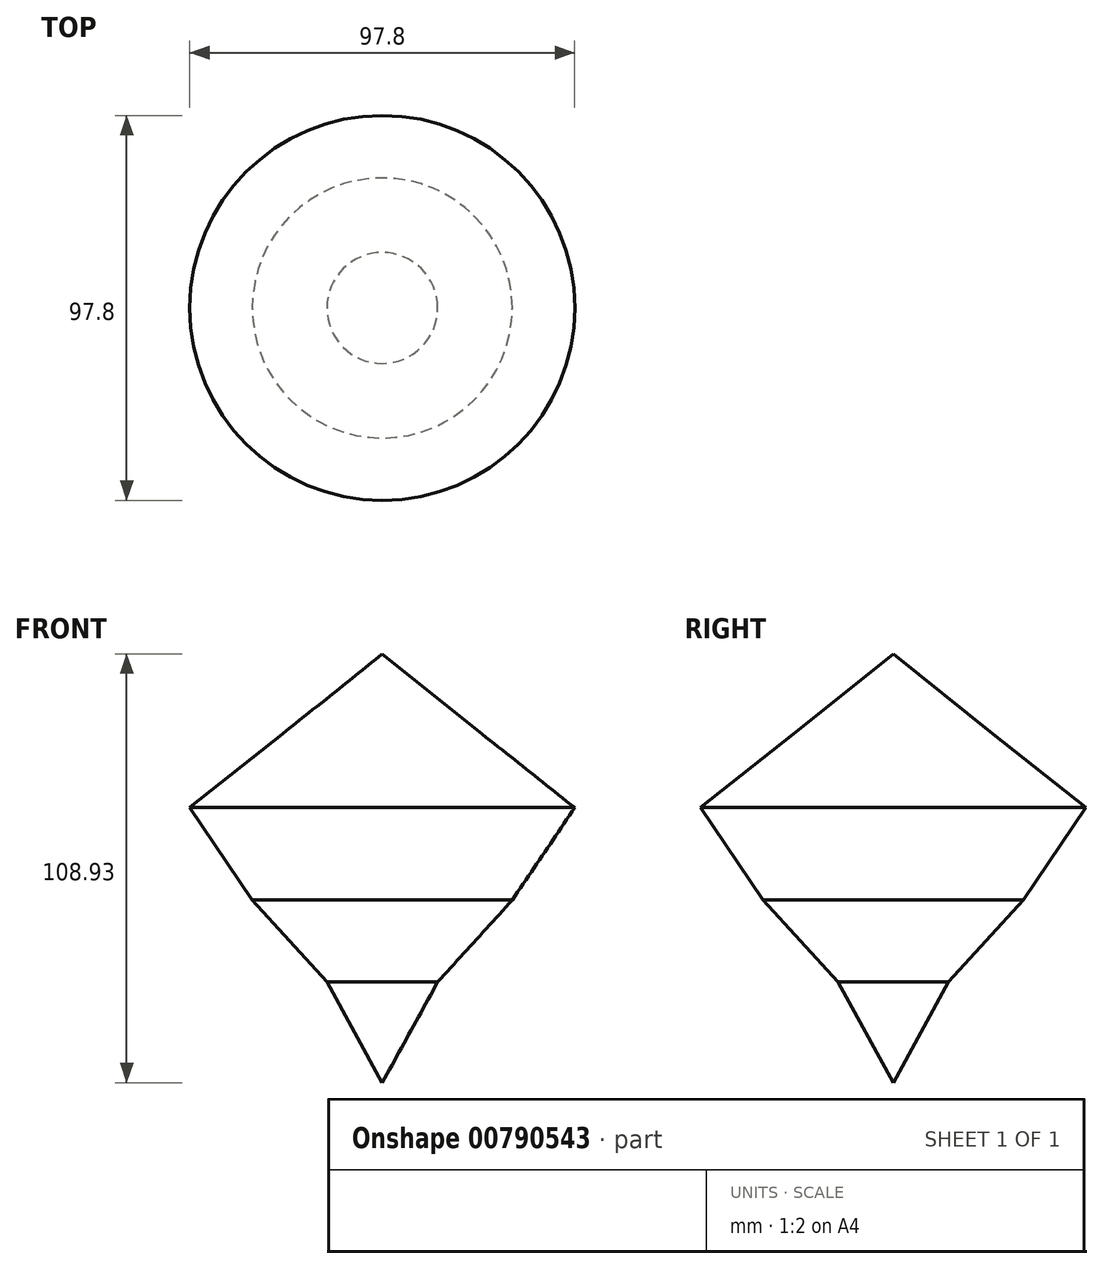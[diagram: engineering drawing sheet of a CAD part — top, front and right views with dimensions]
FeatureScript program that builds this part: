
annotation { "Feature Type Name" : "Feature", "Feature Type Description" : "" }
export const myFeature = defineFeature(function(context is Context, id is Id, definition is map)
    precondition{}
    {
        {
            var Q0;
            Q0=qCreatedBy(makeId("Front.planeOp"),FACE);
            var sketch = newSketch(context, id + "F0", { "sketchPlane" : qUnion([Q0])});
            skLineSegment(sketch, "E0", {"start": v(0, 60.6) * mm, "end": v(0, -48.32) * mm});
            skLineSegment(sketch, "E1", {"start": v(0, 60.6) * mm, "end": v(-25.37, 40.24) * mm});
            skLineSegment(sketch, "E2", {"start": v(-25.37, 40.24) * mm, "end": v(-48.9, 21.56) * mm});
            skLineSegment(sketch, "E3", {"start": v(-48.9, 21.56) * mm, "end": v(-33.03, -1.9) * mm});
            skLineSegment(sketch, "E4", {"start": v(-33.03, -1.9) * mm, "end": v(-14.08, -22.75) * mm});
            skLineSegment(sketch, "E5", {"start": v(-14.08, -22.75) * mm, "end": v(0, -48.32) * mm});
            skSolve(sketch);
        }
        {
            var Q0;
            Q0=makeQuery(id+"F0.imprint","IMPRINT",FACE,{"disambiguationData":[TD([[makeQuery(id+"F0.imprint","IMPRINT",EDGE,{"derivedFrom":sQuery(id+"F0.wireOp",EDGE,"E0")}),-1.0]])]});
            var Q1;
            Q1=sQuery(id+"F0.wireOp",EDGE,"E0");
            revolve(context, id + "F1", {"surfaceOperationType" : NewSurfaceOperationType.NEW, "entities" : qUnion([Q0]), "axis" : qUnion([Q1]), "revolveType" : RevolveType.FULL});
        }
    });
